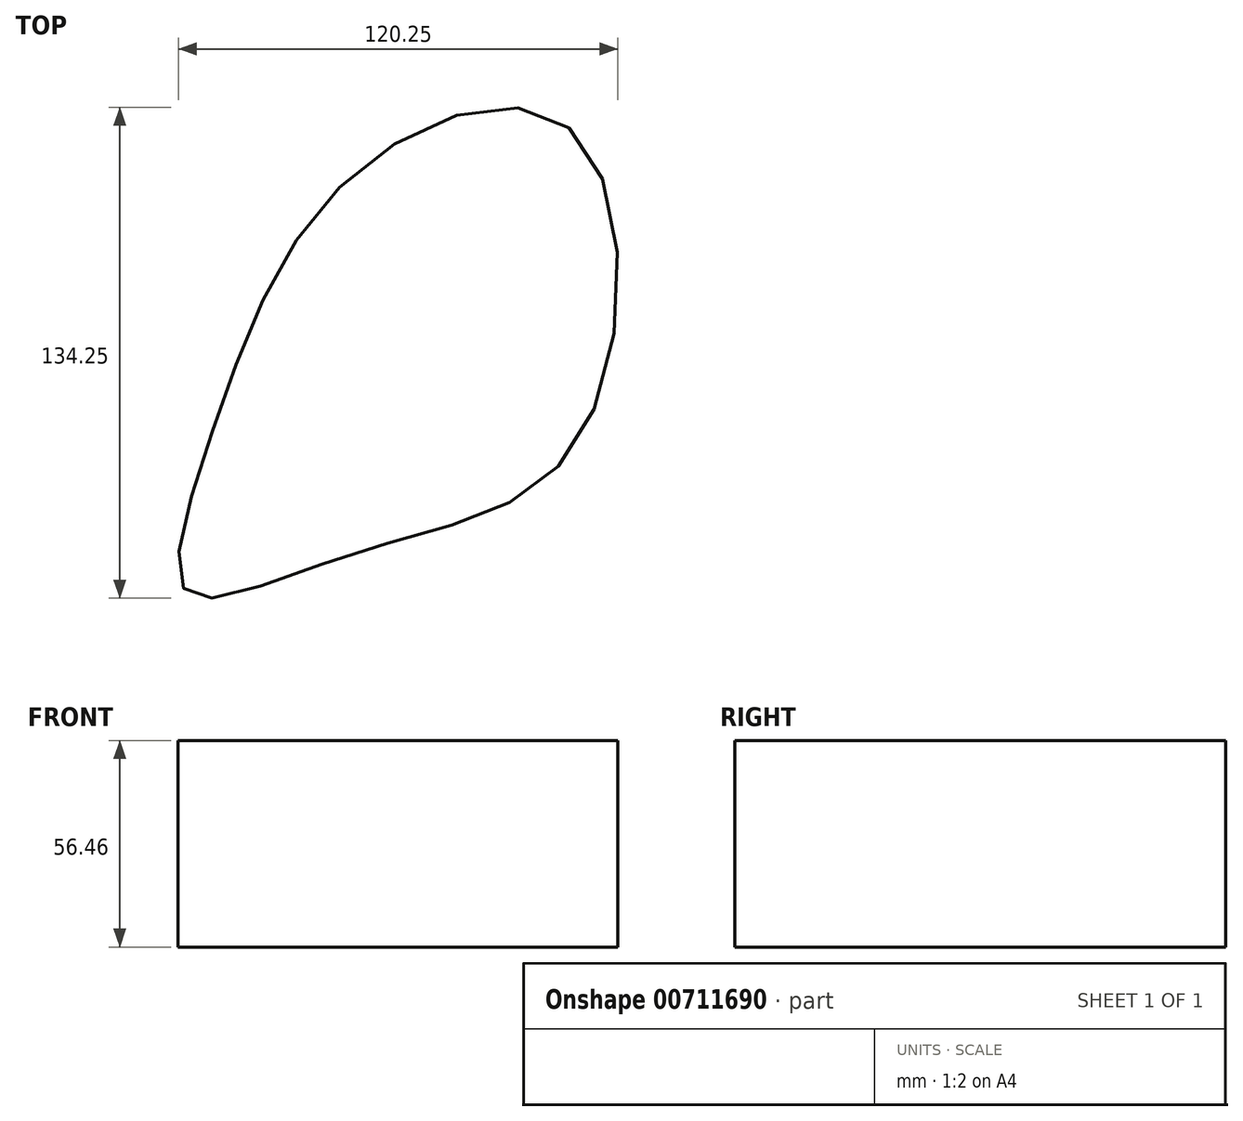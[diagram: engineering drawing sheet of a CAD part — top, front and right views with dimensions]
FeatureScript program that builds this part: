
annotation { "Feature Type Name" : "Feature", "Feature Type Description" : "" }
export const myFeature = defineFeature(function(context is Context, id is Id, definition is map)
    precondition{}
    {
        {
            var Q0;
            Q0=qCreatedBy(makeId("Top.planeOp"),FACE);
            var sketch = newSketch(context, id + "F0", { "sketchPlane" : qUnion([Q0])});
            skFitSpline(sketch, "E0", {"points": [v(-39.57, -45.92) * mm, v(0, 25.32) * mm, v(58.78, 36.45) * mm, v(60.47, -48.49) * mm, v(0, -78.99) * mm, v(-46.34, -90.03) * mm, v(-39.57, -45.92) * mm]});
            skSolve(sketch);
        }
        {
            var Q0;
            Q0=makeQuery(id+"F0.imprint","IMPRINT",FACE,{"disambiguationData":[TD([[makeQuery(id+"F0.imprint","IMPRINT",EDGE,{"derivedFrom":sQuery(id+"F0.wireOp",EDGE,"E0")}),-1.0]])]});
            extrude(context, id + "F1", {"entities" : qUnion([Q0]), "depth" : 56.46 * mm, "offsetDistance" : 25.4 * mm});
        }
    });
